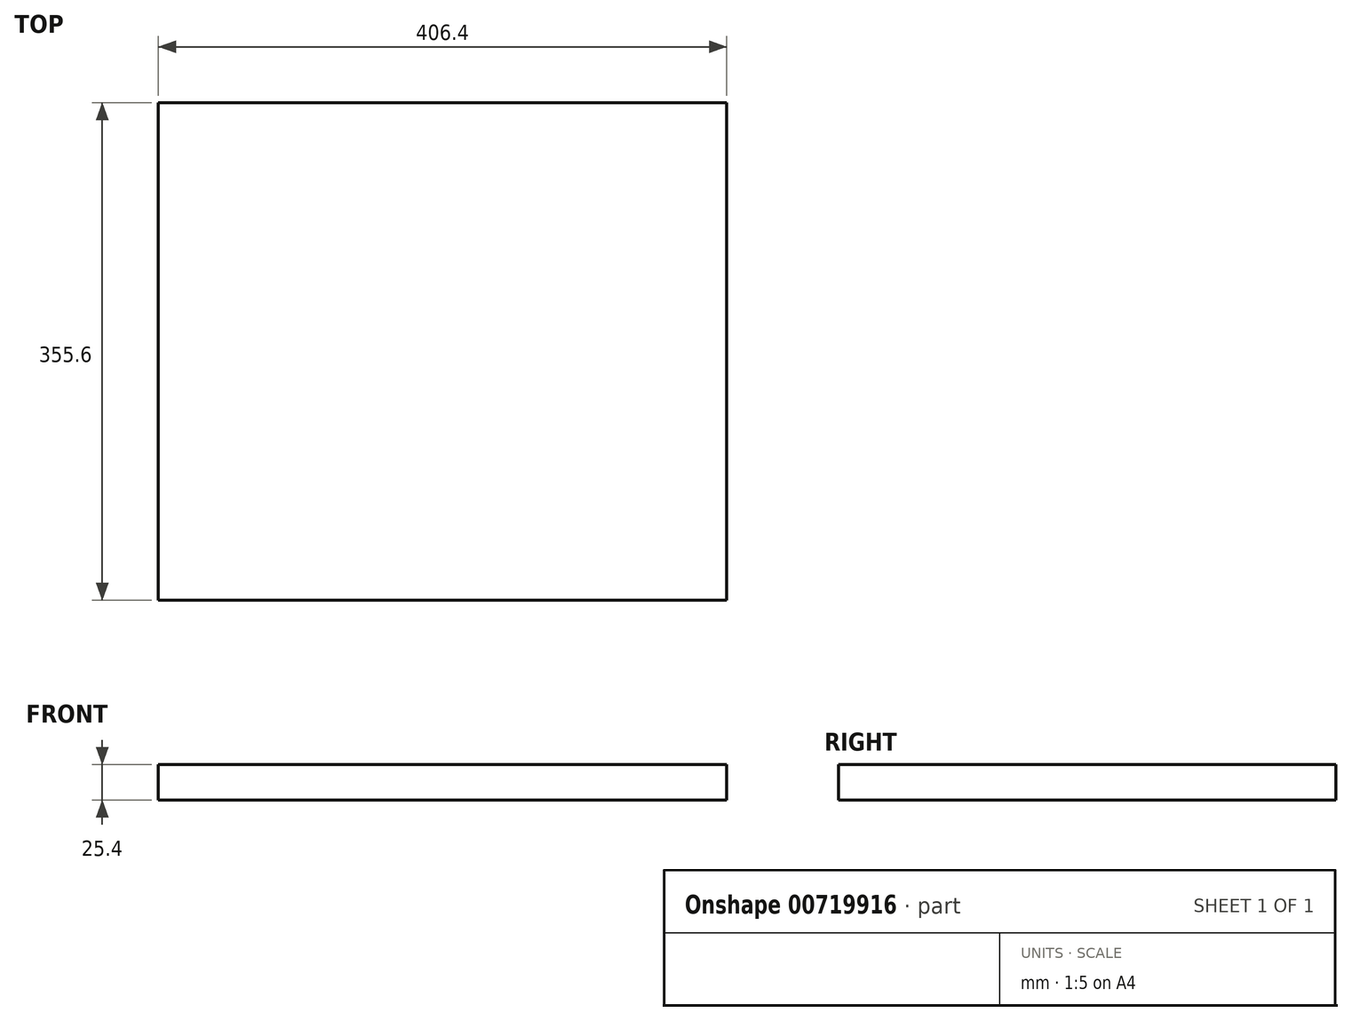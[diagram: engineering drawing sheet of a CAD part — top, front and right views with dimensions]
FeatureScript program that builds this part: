
annotation { "Feature Type Name" : "Feature", "Feature Type Description" : "" }
export const myFeature = defineFeature(function(context is Context, id is Id, definition is map)
    precondition{}
    {
        {
            var Q0;
            Q0=qCreatedBy(makeId("Top.planeOp"),FACE);
            var sketch = newSketch(context, id + "F0", { "sketchPlane" : qUnion([Q0])});
            skLineSegment(sketch, "E0.bottom", {"start": v(212.26, 266.62) * mm, "end": v(-194.14, 266.62) * mm});
            skLineSegment(sketch, "E0.top", {"start": v(212.26, -88.98) * mm, "end": v(-194.14, -88.98) * mm});
            skLineSegment(sketch, "E0.left", {"start": v(212.26, 266.62) * mm, "end": v(212.26, -88.98) * mm});
            skLineSegment(sketch, "E0.right", {"start": v(-194.14, 266.62) * mm, "end": v(-194.14, -88.98) * mm});
            skSolve(sketch);
        }
        {
            var Q0;
            Q0=makeQuery(id+"F0.imprint","IMPRINT",FACE,{"disambiguationData":[TD([[makeQuery(id+"F0.imprint","IMPRINT",EDGE,{"derivedFrom":sQuery(id+"F0.wireOp",EDGE,"E0.bottom")}),1.0]])]});
            extrude(context, id + "F1", {"entities" : qUnion([Q0]), "depth" : 25.4 * mm, "offsetDistance" : 25.4 * mm});
        }
    });
